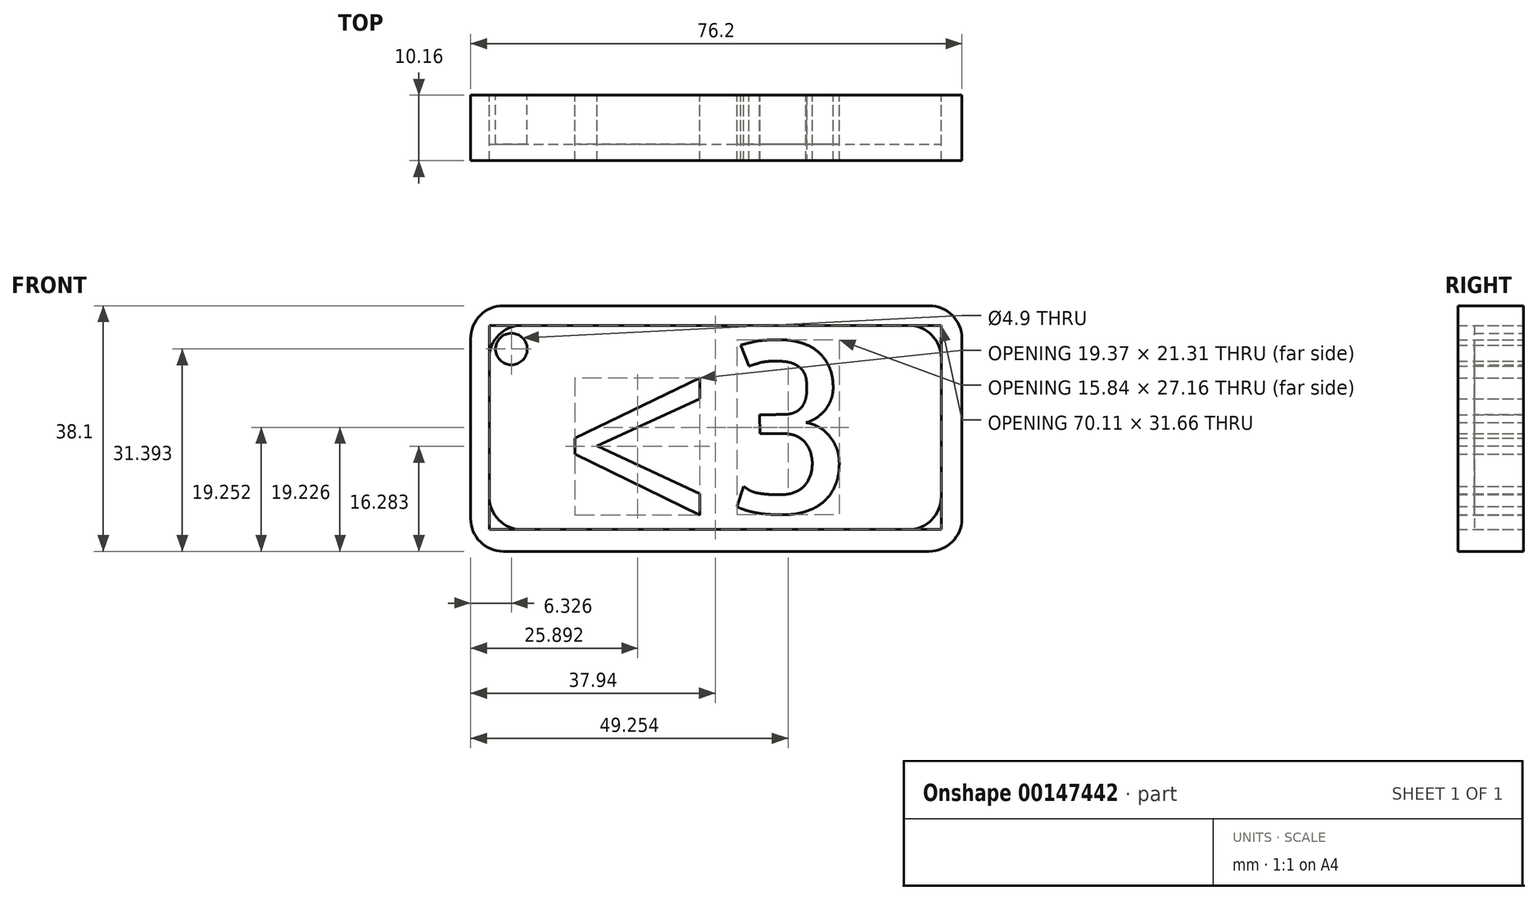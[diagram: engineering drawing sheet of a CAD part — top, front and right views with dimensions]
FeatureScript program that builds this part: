
annotation { "Feature Type Name" : "Feature", "Feature Type Description" : "" }
export const myFeature = defineFeature(function(context is Context, id is Id, definition is map)
    precondition{}
    {
        {
            var Q0;
            Q0=qCreatedBy(makeId("Front.planeOp"),FACE);
            var sketch = newSketch(context, id + "F0", { "sketchPlane" : qUnion([Q0])});
            skLineSegment(sketch, "E0.bottom", {"start": v(-29.27, 8.8) * mm, "end": v(46.93, 8.8) * mm});
            skLineSegment(sketch, "E0.top", {"start": v(-29.27, -29.3) * mm, "end": v(46.93, -29.3) * mm});
            skLineSegment(sketch, "E0.left", {"start": v(-29.27, 8.8) * mm, "end": v(-29.27, -29.3) * mm});
            skLineSegment(sketch, "E0.right", {"start": v(46.93, 8.8) * mm, "end": v(46.93, -29.3) * mm});
            skLineSegment(sketch, "E1.bottom", {"start": v(-26.39, 5.75) * mm, "end": v(43.73, 5.75) * mm});
            skLineSegment(sketch, "E1.top", {"start": v(-26.39, -25.92) * mm, "end": v(43.73, -25.92) * mm});
            skLineSegment(sketch, "E1.left", {"start": v(-26.39, 5.75) * mm, "end": v(-26.39, -25.92) * mm});
            skLineSegment(sketch, "E1.right", {"start": v(43.73, 5.75) * mm, "end": v(43.73, -25.92) * mm});
            skCircle(sketch, "E2", {"center": v(-22.94, 2.08) * mm, "radius": 2.45 * mm});
            skText(sketch, "E3", { "text": "<3", "fontName": "AllertaStencil-Regular.ttf"});
            const initialGuessF0  = {"E3": [-0.01412, -0.02346, 1, 0, 0.02685]};
            skSetInitialGuess(sketch, initialGuessF0);
            skSolve(sketch);
        }
        {
            var Q0;
            Q0=makeQuery(id+"F0.imprint","IMPRINT",FACE,{"disambiguationData":[TD([[makeQuery(id+"F0.imprint","IMPRINT",EDGE,{"derivedFrom":sQuery(id+"F0.wireOp",EDGE,"E0.bottom")}),-1.0]])]});
            extrude(context, id + "F1", {"entities" : qUnion([Q0]), "depth" : 10.16 * mm});
        }
        {
            var Q0;
            Q0=makeQuery(id+"F0.imprint","IMPRINT",FACE,{"disambiguationData":[TD([[makeQuery(id+"F0.imprint","IMPRINT",EDGE,{"derivedFrom":sQuery(id+"F0.wireOp",EDGE,"E3.sketch_text.stroke-0")}),-1.0]])]});
            var Q1;
            Q1=makeQuery(id+"F0.imprint","IMPRINT",FACE,{"disambiguationData":[TD([[makeQuery(id+"F0.imprint","IMPRINT",EDGE,{"derivedFrom":sQuery(id+"F0.wireOp",EDGE,"E3.sketch_text.stroke-7")}),-1.0]])]});
            extrude(context, id + "F2", {"entities" : qUnion([Q0, Q1]), "depth" : 10.16 * mm});
        }
        {
            var Q0;
            Q0=makeQuery(id+"F0.imprint","IMPRINT",FACE,{"disambiguationData":[TD([[makeQuery(id+"F0.imprint","IMPRINT",EDGE,{"derivedFrom":sQuery(id+"F0.wireOp",EDGE,"E1.bottom")}),-1.0]])]});
            extrude(context, id + "F3", {"entities" : qUnion([Q0]), "depth" : 7.62 * mm});
        }
        {
            var Q0;
            Q0=makeQuery(id+"F1.opExtrude","SWEPT_EDGE",EDGE,{"disambiguationData":[OSD([sQuery(id+"F0.wireOp",EDGE,"E0.bottom"),sQuery(id+"F0.wireOp",EDGE,"E0.right")])]});
            var Q1;
            Q1=makeQuery(id+"F1.opExtrude","SWEPT_EDGE",EDGE,{"disambiguationData":[OSD([sQuery(id+"F0.wireOp",EDGE,"E0.top"),sQuery(id+"F0.wireOp",EDGE,"E0.right")])]});
            var Q2;
            Q2=makeQuery(id+"F1.opExtrude","SWEPT_EDGE",EDGE,{"disambiguationData":[OSD([sQuery(id+"F0.wireOp",EDGE,"E0.top"),sQuery(id+"F0.wireOp",EDGE,"E0.left")])]});
            var Q3;
            Q3=makeQuery(id+"F1.opExtrude","SWEPT_EDGE",EDGE,{"disambiguationData":[OSD([sQuery(id+"F0.wireOp",EDGE,"E0.bottom"),sQuery(id+"F0.wireOp",EDGE,"E0.left")])]});
            var Q4;
            Q4=makeQuery(id+"F1.opExtrude","SWEPT_EDGE",EDGE,{"disambiguationData":[OSD([sQuery(id+"F0.wireOp",EDGE,"E1.bottom"),sQuery(id+"F0.wireOp",EDGE,"E1.right")])]});
            var Q5;
            Q5=makeQuery(id+"F1.opExtrude","SWEPT_EDGE",EDGE,{"disambiguationData":[OSD([sQuery(id+"F0.wireOp",EDGE,"E1.bottom"),sQuery(id+"F0.wireOp",EDGE,"E1.left")])]});
            var Q6;
            Q6=makeQuery(id+"F1.opExtrude","SWEPT_EDGE",EDGE,{"disambiguationData":[OSD([sQuery(id+"F0.wireOp",EDGE,"E1.top"),sQuery(id+"F0.wireOp",EDGE,"E1.left")])]});
            var Q7;
            Q7=makeQuery(id+"F1.opExtrude","SWEPT_EDGE",EDGE,{"disambiguationData":[OSD([sQuery(id+"F0.wireOp",EDGE,"E1.top"),sQuery(id+"F0.wireOp",EDGE,"E1.right")])]});
            fillet(context, id + "F4", {"entities" : qUnion([Q0, Q1, Q2, Q3, Q4, Q5, Q6, Q7]), "radius" : 5.08 * mm, "tangentPropagation" : true, "allowEdgeOverflow" : false});
        }
    });
